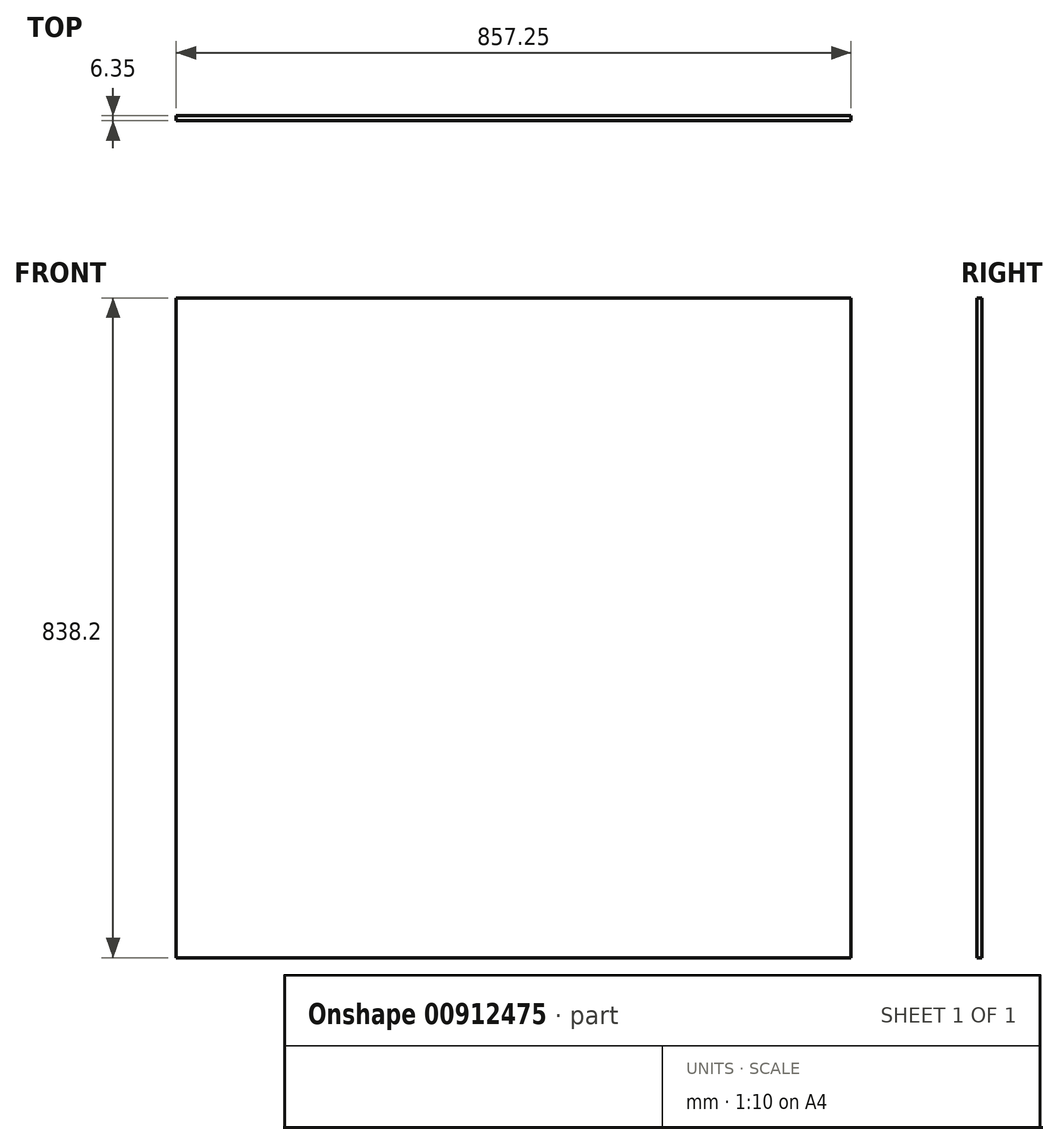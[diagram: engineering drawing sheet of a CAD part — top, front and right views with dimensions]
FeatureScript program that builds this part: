
annotation { "Feature Type Name" : "Feature", "Feature Type Description" : "" }
export const myFeature = defineFeature(function(context is Context, id is Id, definition is map)
    precondition{}
    {
        {
            var Q0;
            Q0=qCreatedBy(makeId("Front.planeOp"),FACE);
            var sketch = newSketch(context, id + "F0", { "sketchPlane" : qUnion([Q0])});
            skLineSegment(sketch, "E0.bottom", {"start": v(0, 0) * mm, "end": v(857.25, 0) * mm});
            skLineSegment(sketch, "E0.top", {"start": v(0, 838.2) * mm, "end": v(857.25, 838.2) * mm});
            skLineSegment(sketch, "E0.left", {"start": v(0, 0) * mm, "end": v(0, 838.2) * mm});
            skLineSegment(sketch, "E0.right", {"start": v(857.25, 0) * mm, "end": v(857.25, 838.2) * mm});
            skSolve(sketch);
        }
        {
            var Q0;
            Q0 = qSketchRegion(id + "F0", true);
            extrude(context, id + "F1", {"entities" : qUnion([Q0]), "depth" : 6.35 * mm, "offsetDistance" : 25.4 * mm});
        }
    });
